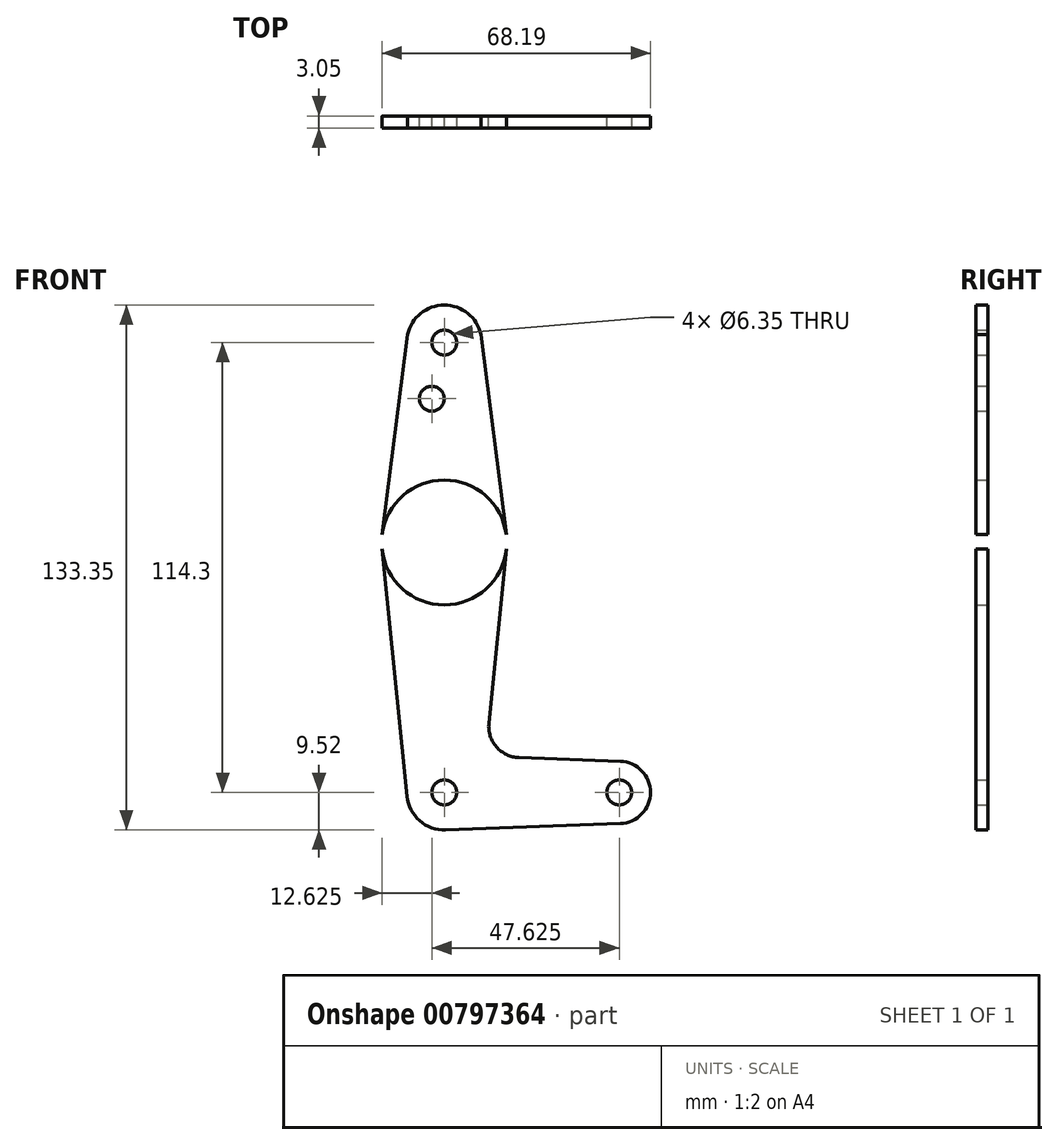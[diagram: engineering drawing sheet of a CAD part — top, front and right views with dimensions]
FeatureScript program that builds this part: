
annotation { "Feature Type Name" : "Feature", "Feature Type Description" : "" }
export const myFeature = defineFeature(function(context is Context, id is Id, definition is map)
    precondition{}
    {
        {
            var Q0;
            Q0=qCreatedBy(makeId("Front.planeOp"),FACE);
            var sketch = newSketch(context, id + "F0", { "sketchPlane" : qUnion([Q0])});
            skLineSegment(sketch, "E0", {"start": v(0, 114.3) * mm, "end": v(0, 0) * mm});
            skLineSegment(sketch, "E1", {"start": v(0, 0) * mm, "end": v(44.45, 0) * mm});
            skCircle(sketch, "E2", {"center": v(0, 114.3) * mm, "radius": 9.53 * mm});
            skCircle(sketch, "E3", {"center": v(44.45, 0) * mm, "radius": 7.94 * mm});
            skCircle(sketch, "E4", {"center": v(0, 0) * mm, "radius": 9.53 * mm});
            skCircle(sketch, "E5", {"center": v(0, 63.5) * mm, "radius": 15.88 * mm});
            skLineSegment(sketch, "E6", {"start": v(9.31, 116.3) * mm, "end": v(15.75, 65.5) * mm});
            skLineSegment(sketch, "E7", {"start": v(15.8, 61.91) * mm, "end": v(11.34, 17.6) * mm});
            skLineSegment(sketch, "E8", {"start": v(18.97, 8.85) * mm, "end": v(44.73, 7.93) * mm});
            skLineSegment(sketch, "E9.MirrorCS", {"start": v(-9.31, 116.3) * mm, "end": v(-15.75, 65.5) * mm});
            skLineSegment(sketch, "E10.MirrorCS", {"start": v(-15.8, 61.91) * mm, "end": v(-9.48, -0.95) * mm});
            skLineSegment(sketch, "E11.MirrorCS", {"start": v(0.34, -9.52) * mm, "end": v(44.73, -7.93) * mm});
            skCircle(sketch, "E12", {"center": v(0, 114.3) * mm, "radius": 3.18 * mm});
            skCircle(sketch, "E13", {"center": v(0, 63.5) * mm, "radius": 3.18 * mm});
            skCircle(sketch, "E14", {"center": v(0, 0) * mm, "radius": 3.18 * mm});
            skCircle(sketch, "E15", {"center": v(44.45, 0) * mm, "radius": 3.18 * mm});
            skCircle(sketch, "E16", {"center": v(-3.17, 100.03) * mm, "radius": 3.18 * mm});
            skPoint(sketch, "E17.newPointA", {"position": v(9.48, -0.95) * mm});
            skPoint(sketch, "E17.newPointB", {"position": v(0.34, 9.52) * mm});
            skArc(sketch, "E17.filletArc", {"start": v(11.34, 17.6) * mm, "mid": v(13.26, 11.57) * mm, "end": v(18.97, 8.85) * mm});
            skSolve(sketch);
        }
        {
            var Q0;
            {var subQ0=sQuery(id+"F0.wireOp",EDGE,"E6");var subQ1=sQuery(id+"F0.wireOp",EDGE,"E2");var subQ2=makeQuery(id+"F0.imprint","INTERSECT",VERTEX,{"disambiguationData":[OD(0.0)],"derivedFrom":[subQ1,subQ0]});Q0=makeQuery(id+"F0.imprint","IMPRINT",FACE,{"disambiguationData":[TD([[makeQuery(id+"F0.imprint","IMPRINT",EDGE,{"disambiguationData":[TD([[subQ2,1.0]])],"derivedFrom":subQ1}),1.0]])]});}
            var Q1;
            {var subQ0=sQuery(id+"F0.wireOp",EDGE,"E9.MirrorCS");var subQ1=sQuery(id+"F0.wireOp",EDGE,"E2");var subQ2=makeQuery(id+"F0.imprint","INTERSECT",VERTEX,{"disambiguationData":[OD(0.0)],"derivedFrom":[subQ1,subQ0]});Q1=makeQuery(id+"F0.imprint","IMPRINT",FACE,{"disambiguationData":[TD([[makeQuery(id+"F0.imprint","IMPRINT",EDGE,{"disambiguationData":[TD([[subQ2,-1.0]])],"derivedFrom":subQ1}),1.0]])]});}
            var Q2;
            {var subQ3=sQuery(id+"F0.wireOp",EDGE,"E0");var subQ5=makeQuery(id+"F0.imprint","INTERSECT",VERTEX,{"derivedFrom":[subQ3,sQuery(id+"F0.wireOp",EDGE,"E16")]});Q2=makeQuery(id+"F0.imprint","IMPRINT",FACE,{"disambiguationData":[TD([[makeQuery(id+"F0.imprint","IMPRINT",EDGE,{"disambiguationData":[TD([[subQ5,1.0]])],"derivedFrom":subQ3}),1.0]])]});}
            var Q3;
            {var subQ5=sQuery(id+"F0.wireOp",EDGE,"E10.MirrorCS");Q3=makeQuery(id+"F0.imprint","IMPRINT",FACE,{"disambiguationData":[TD([[makeQuery(id+"F0.imprint","IMPRINT",EDGE,{"derivedFrom":subQ5}),1.0]])]});}
            var Q4;
            {var subQ5=sQuery(id+"F0.wireOp",EDGE,"E11.MirrorCS");Q4=makeQuery(id+"F0.imprint","IMPRINT",FACE,{"disambiguationData":[TD([[makeQuery(id+"F0.imprint","IMPRINT",EDGE,{"derivedFrom":subQ5}),1.0]])]});}
            var Q5;
            Q5=makeQuery(id+"F0.imprint","IMPRINT",FACE,{"disambiguationData":[TD([[makeQuery(id+"F0.imprint","IMPRINT",EDGE,{"derivedFrom":sQuery(id+"F0.wireOp",EDGE,"E15")}),-1.0]])]});
            var Q6;
            {var subQ8=sQuery(id+"F0.wireOp",EDGE,"E16");Q6=makeQuery(id+"F0.imprint","IMPRINT",FACE,{"disambiguationData":[TD([[makeQuery(id+"F0.imprint","IMPRINT",EDGE,{"derivedFrom":subQ8}),-1.0]])]});}
            var Q7;
            {var subQ0=sQuery(id+"F0.wireOp",EDGE,"E5");var subQ2=sQuery(id+"F0.wireOp",EDGE,"E0");var subQ3=makeQuery(id+"F0.imprint","INTERSECT",VERTEX,{"disambiguationData":[OD(0.0)],"derivedFrom":[subQ2,subQ0]});Q7=makeQuery(id+"F0.imprint","IMPRINT",FACE,{"disambiguationData":[TD([[makeQuery(id+"F0.imprint","IMPRINT",EDGE,{"disambiguationData":[TD([[subQ3,-1.0]])],"derivedFrom":subQ2}),1.0]])]});}
            var Q8;
            {var subQ0=sQuery(id+"F0.wireOp",EDGE,"E5");var subQ3=sQuery(id+"F0.wireOp",EDGE,"E0");var subQ4=makeQuery(id+"F0.imprint","INTERSECT",VERTEX,{"disambiguationData":[OD(0.0)],"derivedFrom":[subQ3,subQ0]});Q8=makeQuery(id+"F0.imprint","IMPRINT",FACE,{"disambiguationData":[TD([[makeQuery(id+"F0.imprint","IMPRINT",EDGE,{"disambiguationData":[TD([[subQ4,-1.0]])],"derivedFrom":subQ3}),-1.0]])]});}
            var Q9;
            {var subQ0=sQuery(id+"F0.wireOp",EDGE,"E4");var subQ2=sQuery(id+"F0.wireOp",EDGE,"E0");var subQ3=makeQuery(id+"F0.imprint","INTERSECT",VERTEX,{"derivedFrom":[subQ2,subQ0]});Q9=makeQuery(id+"F0.imprint","IMPRINT",FACE,{"disambiguationData":[TD([[makeQuery(id+"F0.imprint","IMPRINT",EDGE,{"disambiguationData":[TD([[subQ3,-1.0]])],"derivedFrom":subQ2}),-1.0]])]});}
            var Q10;
            Q10=makeQuery(id+"F0.imprint","IMPRINT",FACE,{"disambiguationData":[TD([[makeQuery(id+"F0.imprint","IMPRINT",EDGE,{"derivedFrom":sQuery(id+"F0.wireOp",EDGE,"E12")}),-1.0]])]});
            var Q11;
            {var subQ10=sQuery(id+"F0.wireOp",EDGE,"E7");Q11=makeQuery(id+"F0.imprint","IMPRINT",FACE,{"disambiguationData":[TD([[makeQuery(id+"F0.imprint","IMPRINT",EDGE,{"derivedFrom":subQ10}),-1.0]])]});}
            var Q12;
            {var subQ0=sQuery(id+"F0.wireOp",EDGE,"E4");var subQ1=sQuery(id+"F0.wireOp",EDGE,"E0");var subQ2=makeQuery(id+"F0.imprint","INTERSECT",VERTEX,{"derivedFrom":[subQ1,subQ0]});Q12=makeQuery(id+"F0.imprint","IMPRINT",FACE,{"disambiguationData":[TD([[makeQuery(id+"F0.imprint","IMPRINT",EDGE,{"disambiguationData":[TD([[subQ2,-1.0]])],"derivedFrom":subQ1}),1.0]])]});}
            extrude(context, id + "F1", {"entities" : qUnion([Q0, Q1, Q2, Q3, Q4, Q5, Q6, Q7, Q8, Q9, Q10, Q11, Q12]), "depth" : 3.05 * mm, "offsetDistance" : 25.4 * mm});
        }
    });
